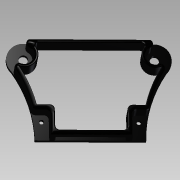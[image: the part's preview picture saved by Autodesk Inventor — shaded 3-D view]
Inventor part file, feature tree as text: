
AUTODESK INVENTOR PART (.ipt)
format: ipt  version: 2015 SP1 (Build 190203100, 203)  size: 724,480 bytes
history: native  units: mm
features: fillet x11, extrude x3, sketch x2
ambient origin geometry x8: Origin, YZ Plane, XZ Plane, XY Plane, X Axis, Y Axis, Z Axis, Center Point
bodies: Solid1 (feature_tree)
feature tree (16):
  sketch  "Sketch1"  dims[d0=3.5mm d18=3.5mm]
  extrude  "Extrusion1"  Depth=3.5mm
  extrude  "Extrusion2"  Depth=3.5mm TaperAngle=0.0deg
  fillet  "Fillet1"  Radius=17.0mm
  fillet  "Fillet2"  Radius=5.0mm
  fillet  "Fillet3"  Radius=5.0mm
  fillet  "Fillet4"  Radius=3.0mm
  fillet  "Fillet5"  Radius=5.0mm
  fillet  "Fillet6"  Radius=3.0mm
  fillet  "Fillet7"  Radius=2.0mm
  fillet  "Fillet8"  Radius=3.0mm
  fillet  "Fillet9"  Radius=0.9mm
  fillet  "Fillet10"  Radius=0.9mm
  extrude  "Extrusion3"  Depth=1.0mm
  fillet  "Fillet11"  Radius=25.0mm
  sketch  "Sketch2"  dims[d19=3.5mm d20=3.5mm d21=0.0mm d22=17.0mm d23=0.0mm d24=5.0mm d25=5.0mm d26=3.0mm d27=5.0mm d28=3.0mm d29=2.0mm d30=3.0mm d31=0.9mm d32=0.9mm d33=0.4mm d34=25.0mm d37=17.0mm d38=0.0mm d39=1.0mm]
